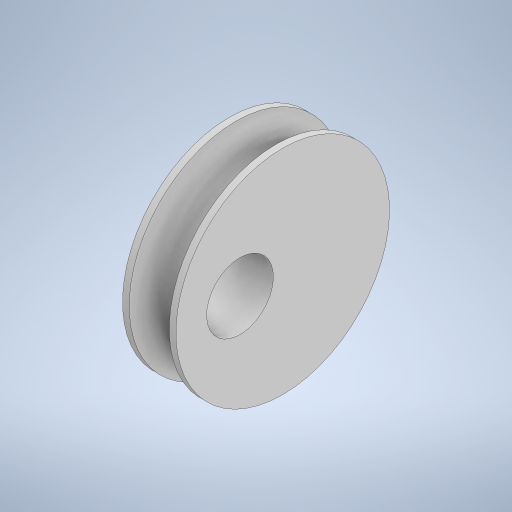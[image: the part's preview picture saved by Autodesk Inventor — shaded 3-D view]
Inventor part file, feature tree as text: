
AUTODESK INVENTOR PART (.ipt)
format: ipt  version: 2023 (Build 270158000, 158)  size: 275,456 bytes
history: native  units: in
note: dims shown in document units (in); Inventor stores cm internally (conversion verified against a paired STEP export)
features: sketch x2, extrude x1, revolve x1
ambient origin geometry x8: Origin, YZ Plane, XZ Plane, XY Plane, X Axis, Y Axis, Z Axis, Center Point
bodies: Solid1 (feature_tree)
feature tree (4):
  extrude  "Extrusion1"  Depth=0.0781in
  revolve  "Revolution1"  [1 undecoded]
  sketch  "Sketch1"  dims[d0=0.25in d1=0.0781in]
  sketch  "Sketch2"  dims[d2=0.05in d3=0.0625in d4=0.0in d5=0.0469in d6=90.0deg]
note: 1 required parameter value undecoded (feature->parameter linkage not recoverable at this tier; creation-order binding heuristic only, values carry confidence <= 0.55)
